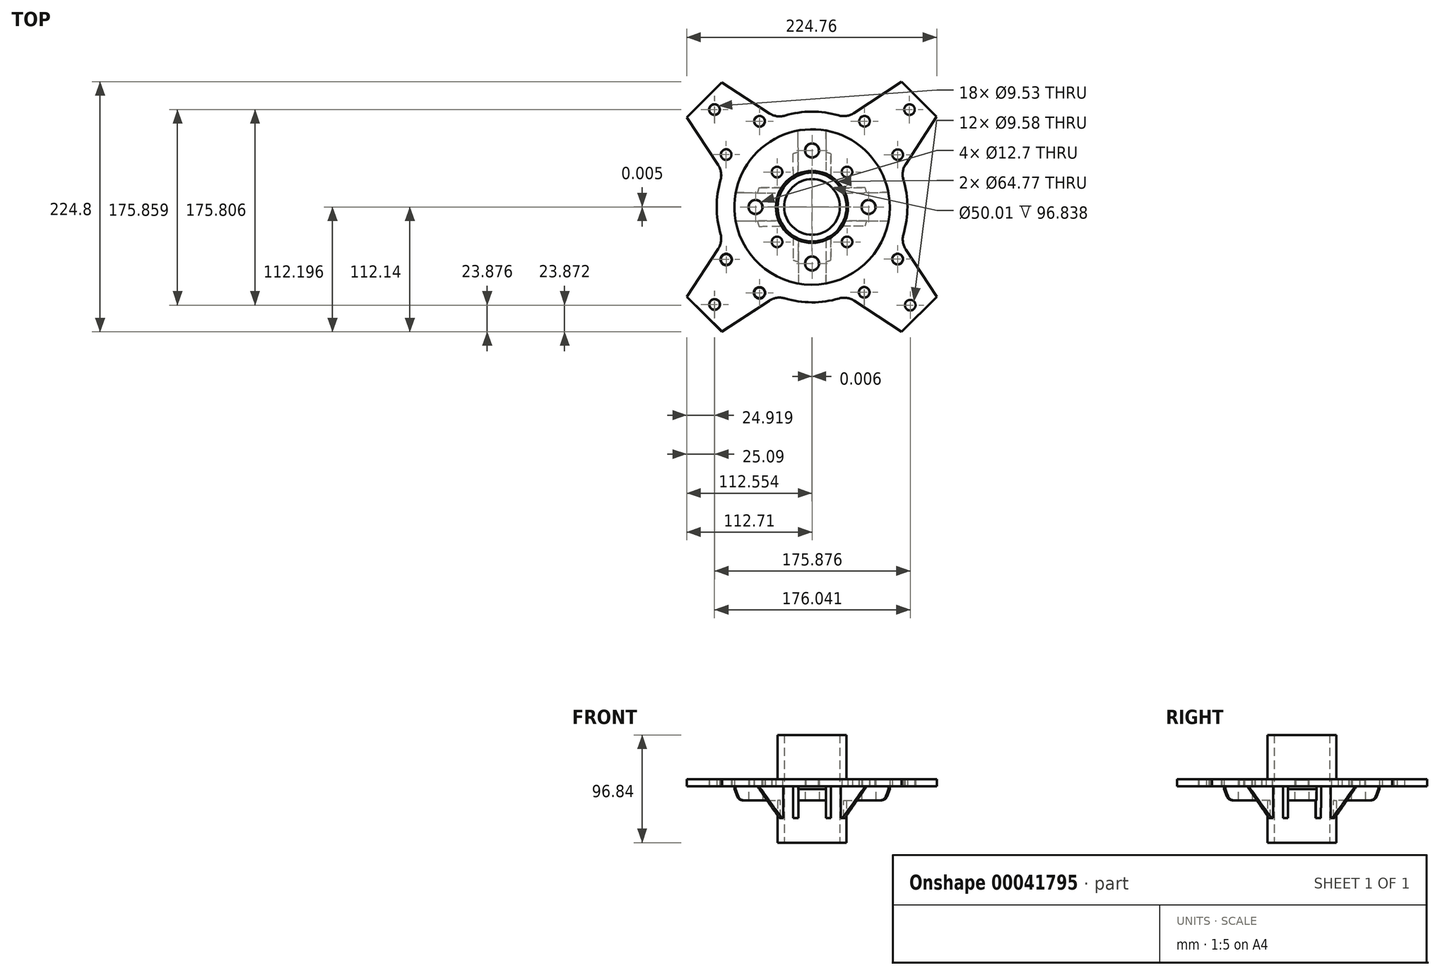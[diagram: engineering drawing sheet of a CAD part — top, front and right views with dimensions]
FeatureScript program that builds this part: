
annotation { "Feature Type Name" : "Feature", "Feature Type Description" : "" }
export const myFeature = defineFeature(function(context is Context, id is Id, definition is map)
    precondition{}
    {
        {
            var Q0;
            Q0=qCreatedBy(makeId("Top.planeOp"),FACE);
            var sketch = newSketch(context, id + "F0", { "sketchPlane" : qUnion([Q0])});
            skCircle(sketch, "E0", {"center": v(0, 0) * mm, "radius": 30.96 * mm});
            skCircle(sketch, "E1", {"center": v(0, 0) * mm, "radius": 25 * mm});
            skCircle(sketch, "E2", {"center": v(0, 0) * mm, "radius": 69.85 * mm});
            skArc(sketch, "E3", {"start": v(-47.7, 17.46) * mm, "mid": v(-48.5, 15.1) * mm, "end": v(-49.19, 12.7) * mm});
            skCircle(sketch, "E4", {"center": v(50.8, 0) * mm, "radius": 6.35 * mm});
            skCircle(sketch, "E5", {"center": v(0, -50.8) * mm, "radius": 6.35 * mm});
            skCircle(sketch, "E6", {"center": v(0, 50.8) * mm, "radius": 6.35 * mm});
            skCircle(sketch, "E7", {"center": v(-50.8, 0) * mm, "radius": 6.35 * mm});
            skArc(sketch, "E8.0", {"start": v(-62.18, 12.9) * mm, "mid": v(-63.5, 0.26) * mm, "end": v(-62.28, -12.38) * mm});
            skLineSegment(sketch, "E9.0", {"start": v(-68.74, -12.38) * mm, "end": v(-28.37, -12.38) * mm});
            skLineSegment(sketch, "E10.0", {"start": v(-68.63, 13) * mm, "end": v(-28.37, 12.38) * mm});
            skLineSegment(sketch, "E11.0", {"start": v(-13, 68.63) * mm, "end": v(-12.38, 28.37) * mm});
            skLineSegment(sketch, "E12.0", {"start": v(12.38, 68.74) * mm, "end": v(12.38, 28.37) * mm});
            skLineSegment(sketch, "E13.trimOffspring", {"start": v(28.37, -12.38) * mm, "end": v(68.74, -12.38) * mm});
            skLineSegment(sketch, "E14.trimOffspring", {"start": v(28.37, 12.38) * mm, "end": v(68.6, 13.19) * mm});
            skLineSegment(sketch, "E15.trimOffspring", {"start": v(12.38, -28.37) * mm, "end": v(12.38, -68.74) * mm});
            skLineSegment(sketch, "E16.trimOffspring", {"start": v(-12.26, -28.42) * mm, "end": v(-12.26, -68.77) * mm});
            skLineSegment(sketch, "E17.0", {"start": v(25.85, 17.04) * mm, "end": v(47.7, 17.48) * mm});
            skLineSegment(sketch, "E18.0", {"start": v(25.85, -17.04) * mm, "end": v(47.86, -17.04) * mm});
            skLineSegment(sketch, "E19.0", {"start": v(17.04, -25.85) * mm, "end": v(17.04, -47.86) * mm});
            skLineSegment(sketch, "E20.0", {"start": v(-17.04, -25.85) * mm, "end": v(-17.04, -47.86) * mm});
            skLineSegment(sketch, "E21.0", {"start": v(17.04, 47.86) * mm, "end": v(17.04, 25.85) * mm});
            skLineSegment(sketch, "E22.trimOffspring", {"start": v(-47.7, 17.46) * mm, "end": v(-25.56, 17.46) * mm});
            skLineSegment(sketch, "E23.trimOffspring", {"start": v(-47.7, -17.48) * mm, "end": v(-25.85, -17.04) * mm});
            skLineSegment(sketch, "E24.trimOffspring", {"start": v(-17.48, 47.7) * mm, "end": v(-17.04, 25.85) * mm});
            skArc(sketch, "E25.trimOffspring", {"start": v(-12.26, -62.3) * mm, "mid": v(0.06, -63.5) * mm, "end": v(12.38, -62.28) * mm});
            skArc(sketch, "E26.trimOffspring", {"start": v(-17.04, -47.86) * mm, "mid": v(-14.67, -48.64) * mm, "end": v(-12.26, -49.3) * mm});
            skArc(sketch, "E27.trimOffspring", {"start": v(62.28, -12.38) * mm, "mid": v(63.5, 0.34) * mm, "end": v(62.14, 13.06) * mm});
            skArc(sketch, "E28.trimOffspring", {"start": v(47.86, -17.04) * mm, "mid": v(48.62, -14.73) * mm, "end": v(49.27, -12.38) * mm});
            skArc(sketch, "E29.trimOffspring", {"start": v(12.38, 62.28) * mm, "mid": v(-0.26, 63.5) * mm, "end": v(-12.9, 62.18) * mm});
            skArc(sketch, "E30.trimOffspring", {"start": v(17.04, 47.86) * mm, "mid": v(14.73, 48.62) * mm, "end": v(12.38, 49.27) * mm});
            skArc(sketch, "E31.trimOffspring", {"start": v(-49.27, -12.38) * mm, "mid": v(-48.55, -14.95) * mm, "end": v(-47.7, -17.48) * mm});
            skArc(sketch, "E32.trimOffspring", {"start": v(12.38, -49.27) * mm, "mid": v(14.73, -48.62) * mm, "end": v(17.04, -47.86) * mm});
            skArc(sketch, "E33.trimOffspring", {"start": v(49.16, 12.8) * mm, "mid": v(48.49, 15.15) * mm, "end": v(47.7, 17.48) * mm});
            skArc(sketch, "E34.trimOffspring", {"start": v(-12.7, 49.19) * mm, "mid": v(-15.1, 48.5) * mm, "end": v(-17.48, 47.7) * mm});
            skSolve(sketch);
        }
        {
            var Q0;
            Q0=qCreatedBy(makeId("Top.planeOp"),FACE);
            var sketch = newSketch(context, id + "F1", { "sketchPlane" : qUnion([Q0])});
            skCircle(sketch, "E35", {"center": v(-77.25, 47.13) * mm, "radius": 4.76 * mm});
            skCircle(sketch, "E36", {"center": v(-0.16, 0.06) * mm, "radius": 32.39 * mm});
            skLineSegment(sketch, "E37", {"start": v(100.22, 100.2) * mm, "end": v(-102.82, -102.8) * mm, "construction": true});
            skCircle(sketch, "E38.0.MirrorC", {"center": v(-47.21, -77.17) * mm, "radius": 5.16 * mm});
            skLineSegment(sketch, "E39", {"start": v(-103.21, 102.97) * mm, "end": v(98.5, -98.33) * mm, "construction": true});
            skCircle(sketch, "E40.0.MirrorC", {"center": v(-77.18, -47.22) * mm, "radius": 5.16 * mm});
            skCircle(sketch, "E41.0.MirrorC", {"center": v(-87.7, -87.7) * mm, "radius": 4.76 * mm});
            skCircle(sketch, "E42", {"center": v(-87.8, 87.6) * mm, "radius": 4.76 * mm});
            skCircle(sketch, "E43", {"center": v(-47.3, 77.09) * mm, "radius": 4.76 * mm});
            skCircle(sketch, "E44", {"center": v(77, 47.02) * mm, "radius": 4.76 * mm});
            skCircle(sketch, "E45", {"center": v(87.56, 87.54) * mm, "radius": 4.76 * mm});
            skCircle(sketch, "E46", {"center": v(47.11, 77.06) * mm, "radius": 4.76 * mm});
            skLineSegment(sketch, "E47", {"start": v(90.92, 90.91) * mm, "end": v(95.62, 95.6) * mm});
            skCircle(sketch, "E48", {"center": v(46.8, -76.66) * mm, "radius": 4.76 * mm});
            skCircle(sketch, "E49", {"center": v(76.84, -46.79) * mm, "radius": 4.76 * mm});
            skCircle(sketch, "E50", {"center": v(88.25, -88.26) * mm, "radius": 4.76 * mm});
            skLineSegment(sketch, "E51", {"start": v(80.53, -112.13) * mm, "end": v(112.05, -80.8) * mm});
            skPoint(sketch, "E52", {"position": v(-81.28, -112.08) * mm});
            skPoint(sketch, "E53", {"position": v(-112.71, -80.65) * mm});
            skLineSegment(sketch, "E54", {"start": v(-112.71, -80.65) * mm, "end": v(-81.28, -112.08) * mm});
            skPoint(sketch, "E55", {"position": v(-112.67, 80.67) * mm});
            skPoint(sketch, "E56", {"position": v(-81.24, 112.1) * mm});
            skLineSegment(sketch, "E57", {"start": v(-81.24, 112.1) * mm, "end": v(-112.67, 80.67) * mm});
            skPoint(sketch, "E58", {"position": v(80.48, 112.66) * mm});
            skLineSegment(sketch, "E59", {"start": v(80.48, 112.66) * mm, "end": v(111.83, 81.15) * mm});
            skPoint(sketch, "E60", {"position": v(111.83, 81.15) * mm});
            skPoint(sketch, "E61", {"position": v(112.05, -80.8) * mm});
            skPoint(sketch, "E62", {"position": v(80.53, -112.13) * mm});
            skCircle(sketch, "E63", {"center": v(-0.16, 0.06) * mm, "radius": 50.8 * mm, "construction": true});
            skLineSegment(sketch, "E64", {"start": v(0, -85.66) * mm, "end": v(0, 97.9) * mm, "construction": true});
            skLineSegment(sketch, "E65", {"start": v(-85.88, 0) * mm, "end": v(116, 0) * mm, "construction": true});
            skLineSegment(sketch, "E66", {"start": v(112.05, -80.8) * mm, "end": v(84.2, -38.16) * mm});
            skLineSegment(sketch, "E67", {"start": v(80.53, -112.13) * mm, "end": v(37.93, -84.28) * mm});
            skLineSegment(sketch, "E68", {"start": v(-112.67, 80.67) * mm, "end": v(-84.39, 37.74) * mm});
            skLineSegment(sketch, "E69", {"start": v(-38.3, 84.15) * mm, "end": v(-81.24, 112.1) * mm});
            skLineSegment(sketch, "E70", {"start": v(80.48, 112.66) * mm, "end": v(37.56, 84.43) * mm});
            skLineSegment(sketch, "E71", {"start": v(-112.71, -80.65) * mm, "end": v(-84.42, -37.59) * mm});
            skLineSegment(sketch, "E72", {"start": v(-81.28, -112.08) * mm, "end": v(-38.38, -84.13) * mm});
            skLineSegment(sketch, "E73", {"start": v(84.1, 38.46) * mm, "end": v(111.83, 81.15) * mm});
            skArc(sketch, "E74", {"start": v(-24.55, -82.13) * mm, "mid": v(-0.2, -85.72) * mm, "end": v(24.16, -82.25) * mm});
            skArc(sketch, "E75.trimOffspring", {"start": v(-82.3, 23.96) * mm, "mid": v(-85.72, 0.06) * mm, "end": v(-82.34, -23.85) * mm});
            skArc(sketch, "E76.filletArc", {"start": v(-82.3, 23.96) * mm, "mid": v(-81.83, 31.08) * mm, "end": v(-84.39, 37.74) * mm});
            skArc(sketch, "E77.filletArc", {"start": v(-84.42, -37.59) * mm, "mid": v(-81.87, -30.95) * mm, "end": v(-82.34, -23.85) * mm});
            skArc(sketch, "E78.filletArc", {"start": v(-24.55, -82.13) * mm, "mid": v(-31.69, -81.6) * mm, "end": v(-38.38, -84.13) * mm});
            skArc(sketch, "E79.trimOffspring", {"start": v(23.82, 82.35) * mm, "mid": v(-0.35, 85.72) * mm, "end": v(-24.49, 82.15) * mm});
            skArc(sketch, "E80.trimOffspring", {"start": v(82.2, -24.36) * mm, "mid": v(85.72, 0.15) * mm, "end": v(82.1, 24.64) * mm});
            skArc(sketch, "E81.filletArc", {"start": v(37.93, -84.28) * mm, "mid": v(31.27, -81.76) * mm, "end": v(24.16, -82.25) * mm});
            skArc(sketch, "E82.filletArc", {"start": v(82.2, -24.36) * mm, "mid": v(81.68, -31.48) * mm, "end": v(84.2, -38.16) * mm});
            skArc(sketch, "E83.filletArc", {"start": v(84.1, 38.46) * mm, "mid": v(81.58, 31.77) * mm, "end": v(82.1, 24.64) * mm});
            skArc(sketch, "E84.filletArc", {"start": v(23.82, 82.35) * mm, "mid": v(30.92, 81.88) * mm, "end": v(37.56, 84.43) * mm});
            skArc(sketch, "E85.filletArc", {"start": v(-38.3, 84.15) * mm, "mid": v(-31.6, 81.63) * mm, "end": v(-24.49, 82.15) * mm});
            skCircle(sketch, "E86", {"center": v(0, 0) * mm, "radius": 44.45 * mm, "construction": true});
            skPoint(sketch, "E87", {"position": v(31.45, -31.42) * mm});
            skPoint(sketch, "E88", {"position": v(-31.43, -31.43) * mm});
            skPoint(sketch, "E89", {"position": v(31.43, 31.43) * mm});
            skPoint(sketch, "E90", {"position": v(-31.48, 31.38) * mm});
            skCircle(sketch, "E91", {"center": v(-31.48, 31.38) * mm, "radius": 4.76 * mm});
            skCircle(sketch, "E92", {"center": v(31.45, -31.42) * mm, "radius": 4.76 * mm});
            skCircle(sketch, "E93", {"center": v(31.43, 31.43) * mm, "radius": 4.76 * mm});
            skCircle(sketch, "E94", {"center": v(-31.43, -31.45) * mm, "radius": 4.76 * mm});
            skCircle(sketch, "E95", {"center": v(0, 0) * mm, "radius": 123.83 * mm, "construction": true});
            skCircle(sketch, "E96", {"center": v(0, 0) * mm, "radius": 136.53 * mm, "construction": true});
            skCircle(sketch, "E97", {"center": v(0, 0) * mm, "radius": 90.49 * mm, "construction": true});
            skSolve(sketch);
        }
        {
            var Q0;
            Q0=qCreatedBy(makeId("Top.planeOp"),FACE);
            var sketch = newSketch(context, id + "F2", { "sketchPlane" : qUnion([Q0])});
            skCircle(sketch, "E98", {"center": v(-0.15, 0.06) * mm, "radius": 32.39 * mm});
            skLineSegment(sketch, "E99", {"start": v(100.23, 100.2) * mm, "end": v(-102.81, -102.81) * mm, "construction": true});
            skLineSegment(sketch, "E100", {"start": v(-119.3, 119.07) * mm, "end": v(108.26, -108) * mm, "construction": true});
            skLineSegment(sketch, "E101", {"start": v(90.93, 90.9) * mm, "end": v(93.76, 93.73) * mm});
            skLineSegment(sketch, "E102", {"start": v(80.53, -112.14) * mm, "end": v(112.05, -80.8) * mm});
            skPoint(sketch, "E103", {"position": v(-80.94, -111.87) * mm});
            skPoint(sketch, "E104", {"position": v(-112.71, -80.67) * mm});
            skLineSegment(sketch, "E105", {"start": v(-112.71, -80.67) * mm, "end": v(-80.94, -111.87) * mm});
            skPoint(sketch, "E106", {"position": v(-112.5, 80.56) * mm});
            skPoint(sketch, "E107", {"position": v(-81.07, 112) * mm});
            skLineSegment(sketch, "E108", {"start": v(-81.07, 112) * mm, "end": v(-112.5, 80.56) * mm});
            skPoint(sketch, "E109", {"position": v(80.49, 112.66) * mm});
            skLineSegment(sketch, "E110", {"start": v(80.49, 112.66) * mm, "end": v(111.84, 81.15) * mm});
            skCircle(sketch, "E111", {"center": v(0, 50.8) * mm, "radius": 5.56 * mm});
            skCircle(sketch, "E112", {"center": v(50.8, 0) * mm, "radius": 5.56 * mm});
            skCircle(sketch, "E113", {"center": v(0, -50.8) * mm, "radius": 5.56 * mm});
            skCircle(sketch, "E114", {"center": v(-50.8, 0) * mm, "radius": 5.56 * mm});
            skPoint(sketch, "E115", {"position": v(111.84, 81.15) * mm});
            skPoint(sketch, "E116", {"position": v(112.05, -80.8) * mm});
            skPoint(sketch, "E117", {"position": v(80.53, -112.14) * mm});
            skCircle(sketch, "E118", {"center": v(-0.15, 0.06) * mm, "radius": 50.8 * mm, "construction": true});
            skLineSegment(sketch, "E119", {"start": v(0, -85.67) * mm, "end": v(0, 97.9) * mm, "construction": true});
            skLineSegment(sketch, "E120", {"start": v(-85.87, 0) * mm, "end": v(116.01, 0) * mm, "construction": true});
            skLineSegment(sketch, "E121", {"start": v(112.05, -80.8) * mm, "end": v(84.22, -38.16) * mm});
            skLineSegment(sketch, "E122", {"start": v(80.53, -112.14) * mm, "end": v(37.94, -84.29) * mm});
            skLineSegment(sketch, "E123", {"start": v(-112.5, 80.56) * mm, "end": v(-84.37, 37.72) * mm});
            skLineSegment(sketch, "E124", {"start": v(-38.29, 84.15) * mm, "end": v(-81.07, 112) * mm});
            skLineSegment(sketch, "E125", {"start": v(80.49, 112.66) * mm, "end": v(37.57, 84.43) * mm});
            skLineSegment(sketch, "E126", {"start": v(-112.71, -80.67) * mm, "end": v(-84.4, -37.6) * mm});
            skLineSegment(sketch, "E127", {"start": v(-80.94, -111.87) * mm, "end": v(-38.37, -84.14) * mm});
            skLineSegment(sketch, "E128", {"start": v(84.1, 38.46) * mm, "end": v(111.84, 81.15) * mm});
            skArc(sketch, "E129", {"start": v(-24.55, -82.14) * mm, "mid": v(-0.2, -85.73) * mm, "end": v(24.17, -82.25) * mm});
            skArc(sketch, "E130.trimOffspring", {"start": v(-82.3, 23.96) * mm, "mid": v(-85.72, 0.06) * mm, "end": v(-82.34, -23.85) * mm});
            skArc(sketch, "E131.filletArc", {"start": v(-82.3, 23.96) * mm, "mid": v(-81.82, 31.06) * mm, "end": v(-84.37, 37.72) * mm});
            skArc(sketch, "E132.filletArc", {"start": v(-84.4, -37.6) * mm, "mid": v(-81.87, -30.95) * mm, "end": v(-82.34, -23.85) * mm});
            skArc(sketch, "E133.filletArc", {"start": v(-24.55, -82.14) * mm, "mid": v(-31.68, -81.61) * mm, "end": v(-38.37, -84.14) * mm});
            skArc(sketch, "E134.trimOffspring", {"start": v(23.82, 82.35) * mm, "mid": v(-0.34, 85.72) * mm, "end": v(-24.48, 82.15) * mm});
            skArc(sketch, "E135.trimOffspring", {"start": v(82.2, -24.36) * mm, "mid": v(85.73, 0.14) * mm, "end": v(82.12, 24.63) * mm});
            skArc(sketch, "E136.filletArc", {"start": v(37.94, -84.29) * mm, "mid": v(31.27, -81.76) * mm, "end": v(24.17, -82.25) * mm});
            skArc(sketch, "E137.filletArc", {"start": v(82.2, -24.36) * mm, "mid": v(81.69, -31.48) * mm, "end": v(84.22, -38.16) * mm});
            skArc(sketch, "E138.filletArc", {"start": v(84.1, 38.46) * mm, "mid": v(81.58, 31.76) * mm, "end": v(82.12, 24.63) * mm});
            skArc(sketch, "E139.filletArc", {"start": v(23.82, 82.35) * mm, "mid": v(30.92, 81.88) * mm, "end": v(37.57, 84.43) * mm});
            skArc(sketch, "E140.filletArc", {"start": v(-38.29, 84.15) * mm, "mid": v(-31.6, 81.63) * mm, "end": v(-24.48, 82.15) * mm});
            skCircle(sketch, "E141", {"center": v(0, 50.8) * mm, "radius": 6.35 * mm});
            skCircle(sketch, "E142", {"center": v(-50.8, 0) * mm, "radius": 6.35 * mm});
            skCircle(sketch, "E143", {"center": v(0, -50.8) * mm, "radius": 6.35 * mm});
            skCircle(sketch, "E144", {"center": v(50.8, 0) * mm, "radius": 6.35 * mm});
            skCircle(sketch, "E145", {"center": v(-77.24, 47.12) * mm, "radius": 4.79 * mm});
            skCircle(sketch, "E146", {"center": v(-77.17, -47.22) * mm, "radius": 4.79 * mm});
            skCircle(sketch, "E147", {"center": v(-47.2, -77.17) * mm, "radius": 4.79 * mm});
            skCircle(sketch, "E148", {"center": v(46.95, -76.76) * mm, "radius": 4.79 * mm});
            skCircle(sketch, "E149", {"center": v(77, -46.88) * mm, "radius": 4.79 * mm});
            skCircle(sketch, "E150", {"center": v(77, 47.02) * mm, "radius": 4.79 * mm});
            skCircle(sketch, "E151", {"center": v(88.26, -88.27) * mm, "radius": 4.79 * mm});
            skCircle(sketch, "E152", {"center": v(-87.54, -87.58) * mm, "radius": 4.79 * mm});
            skCircle(sketch, "E153", {"center": v(-87.62, 87.48) * mm, "radius": 4.79 * mm});
            skCircle(sketch, "E154", {"center": v(-47.14, 77) * mm, "radius": 4.79 * mm});
            skCircle(sketch, "E155", {"center": v(47.12, 77.05) * mm, "radius": 4.79 * mm});
            skCircle(sketch, "E156", {"center": v(87.56, 87.54) * mm, "radius": 4.79 * mm});
            skCircle(sketch, "E157", {"center": v(0, 0) * mm, "radius": 44.45 * mm, "construction": true});
            skPoint(sketch, "E158", {"position": v(-31.45, 31.4) * mm});
            skPoint(sketch, "E159", {"position": v(31.44, 31.42) * mm});
            skPoint(sketch, "E160", {"position": v(31.48, -31.4) * mm});
            skPoint(sketch, "E161", {"position": v(-31.43, -31.44) * mm});
            skCircle(sketch, "E162", {"center": v(31.43, 31.43) * mm, "radius": 4.76 * mm});
            skCircle(sketch, "E163", {"center": v(-31.45, 31.4) * mm, "radius": 4.76 * mm});
            skCircle(sketch, "E164", {"center": v(-31.43, -31.43) * mm, "radius": 4.76 * mm});
            skCircle(sketch, "E165", {"center": v(31.48, -31.4) * mm, "radius": 4.76 * mm});
            skCircle(sketch, "E166", {"center": v(0, 0) * mm, "radius": 90.49 * mm, "construction": true});
            skCircle(sketch, "E167", {"center": v(0, 0) * mm, "radius": 123.83 * mm, "construction": true});
            skCircle(sketch, "E168", {"center": v(0, 0) * mm, "radius": 136.53 * mm, "construction": true});
            skPoint(sketch, "E169", {"position": v(-96.62, 96.45) * mm});
            skPoint(sketch, "E170", {"position": v(96.5, -96.27) * mm});
            skSolve(sketch);
        }
        {
            var Q0;
            {var subQ4=sQuery(id+"F0.wireOp",EDGE,"E3");Q0=makeQuery(id+"F0.imprint","IMPRINT",FACE,{"disambiguationData":[TD([[makeQuery(id+"F0.imprint","IMPRINT",EDGE,{"derivedFrom":subQ4}),-1.0]])]});}
            var Q1;
            {var subQ3=sQuery(id+"F0.wireOp",EDGE,"E8.0");Q1=makeQuery(id+"F0.imprint","IMPRINT",FACE,{"disambiguationData":[TD([[makeQuery(id+"F0.imprint","IMPRINT",EDGE,{"derivedFrom":subQ3}),-1.0]])]});}
            var Q2;
            {var subQ10=sQuery(id+"F0.wireOp",EDGE,"E20.0");Q2=makeQuery(id+"F0.imprint","IMPRINT",FACE,{"disambiguationData":[TD([[makeQuery(id+"F0.imprint","IMPRINT",EDGE,{"derivedFrom":subQ10}),-1.0]])]});}
            var Q3;
            {var subQ0=sQuery(id+"F0.wireOp",EDGE,"E25.trimOffspring");Q3=makeQuery(id+"F0.imprint","IMPRINT",FACE,{"disambiguationData":[TD([[makeQuery(id+"F0.imprint","IMPRINT",EDGE,{"derivedFrom":subQ0}),-1.0]])]});}
            var Q4;
            {var subQ2=sQuery(id+"F0.wireOp",EDGE,"E18.0");Q4=makeQuery(id+"F0.imprint","IMPRINT",FACE,{"disambiguationData":[TD([[makeQuery(id+"F0.imprint","IMPRINT",EDGE,{"derivedFrom":subQ2}),-1.0]])]});}
            var Q5;
            {var subQ0=sQuery(id+"F0.wireOp",EDGE,"E27.trimOffspring");Q5=makeQuery(id+"F0.imprint","IMPRINT",FACE,{"disambiguationData":[TD([[makeQuery(id+"F0.imprint","IMPRINT",EDGE,{"derivedFrom":subQ0}),-1.0]])]});}
            var Q6;
            {var subQ3=sQuery(id+"F0.wireOp",EDGE,"E17.0");Q6=makeQuery(id+"F0.imprint","IMPRINT",FACE,{"disambiguationData":[TD([[makeQuery(id+"F0.imprint","IMPRINT",EDGE,{"derivedFrom":subQ3}),1.0]])]});}
            var Q7;
            {var subQ0=sQuery(id+"F0.wireOp",EDGE,"E29.trimOffspring");Q7=makeQuery(id+"F0.imprint","IMPRINT",FACE,{"disambiguationData":[TD([[makeQuery(id+"F0.imprint","IMPRINT",EDGE,{"derivedFrom":subQ0}),-1.0]])]});}
            var Q8;
            Q8=makeQuery(id+"F0.imprint","IMPRINT",FACE,{"disambiguationData":[TD([[makeQuery(id+"F0.imprint","IMPRINT",EDGE,{"derivedFrom":sQuery(id+"F0.wireOp",EDGE,"E7")}),-1.0]])]});
            var Q9;
            Q9=makeQuery(id+"F0.imprint","IMPRINT",FACE,{"disambiguationData":[TD([[makeQuery(id+"F0.imprint","IMPRINT",EDGE,{"derivedFrom":sQuery(id+"F0.wireOp",EDGE,"E6")}),-1.0]])]});
            var Q10;
            Q10=makeQuery(id+"F0.imprint","IMPRINT",FACE,{"disambiguationData":[TD([[makeQuery(id+"F0.imprint","IMPRINT",EDGE,{"derivedFrom":sQuery(id+"F0.wireOp",EDGE,"E4")}),-1.0]])]});
            var Q11;
            Q11=makeQuery(id+"F0.imprint","IMPRINT",FACE,{"disambiguationData":[TD([[makeQuery(id+"F0.imprint","IMPRINT",EDGE,{"derivedFrom":sQuery(id+"F0.wireOp",EDGE,"E5")}),-1.0]])]});
            var Q12;
            {var subQ3=sQuery(id+"F0.wireOp",EDGE,"E3");Q12=makeQuery(id+"F0.imprint","IMPRINT",FACE,{"disambiguationData":[TD([[makeQuery(id+"F0.imprint","IMPRINT",EDGE,{"derivedFrom":subQ3}),1.0]])]});}
            var Q13;
            {var subQ1=sQuery(id+"F0.wireOp",EDGE,"E23.trimOffspring");Q13=makeQuery(id+"F0.imprint","IMPRINT",FACE,{"disambiguationData":[TD([[makeQuery(id+"F0.imprint","IMPRINT",EDGE,{"derivedFrom":subQ1}),1.0]])]});}
            var Q14;
            {var subQ1=sQuery(id+"F0.wireOp",EDGE,"E20.0");Q14=makeQuery(id+"F0.imprint","IMPRINT",FACE,{"disambiguationData":[TD([[makeQuery(id+"F0.imprint","IMPRINT",EDGE,{"derivedFrom":subQ1}),1.0]])]});}
            var Q15;
            {var subQ0=sQuery(id+"F0.wireOp",EDGE,"E19.0");Q15=makeQuery(id+"F0.imprint","IMPRINT",FACE,{"disambiguationData":[TD([[makeQuery(id+"F0.imprint","IMPRINT",EDGE,{"derivedFrom":subQ0}),-1.0]])]});}
            var Q16;
            {var subQ1=sQuery(id+"F0.wireOp",EDGE,"E18.0");Q16=makeQuery(id+"F0.imprint","IMPRINT",FACE,{"disambiguationData":[TD([[makeQuery(id+"F0.imprint","IMPRINT",EDGE,{"derivedFrom":subQ1}),1.0]])]});}
            var Q17;
            {var subQ1=sQuery(id+"F0.wireOp",EDGE,"E17.0");Q17=makeQuery(id+"F0.imprint","IMPRINT",FACE,{"disambiguationData":[TD([[makeQuery(id+"F0.imprint","IMPRINT",EDGE,{"derivedFrom":subQ1}),-1.0]])]});}
            var Q18;
            {var subQ1=sQuery(id+"F0.wireOp",EDGE,"E21.0");Q18=makeQuery(id+"F0.imprint","IMPRINT",FACE,{"disambiguationData":[TD([[makeQuery(id+"F0.imprint","IMPRINT",EDGE,{"derivedFrom":subQ1}),-1.0]])]});}
            var Q19;
            {var subQ1=sQuery(id+"F0.wireOp",EDGE,"E24.trimOffspring");Q19=makeQuery(id+"F0.imprint","IMPRINT",FACE,{"disambiguationData":[TD([[makeQuery(id+"F0.imprint","IMPRINT",EDGE,{"derivedFrom":subQ1}),1.0]])]});}
            var Q20;
            Q20=makeQuery(id+"F0.imprint","IMPRINT",FACE,{"disambiguationData":[TD([[makeQuery(id+"F0.imprint","IMPRINT",EDGE,{"derivedFrom":sQuery(id+"F0.wireOp",EDGE,"E1")}),-1.0]])]});
            extrude(context, id + "F3", {"entities" : qUnion([Q0, Q1, Q2, Q3, Q4, Q5, Q6, Q7, Q8, Q9, Q10, Q11, Q12, Q13, Q14, Q15, Q16, Q17, Q18, Q19, Q20]), "depth" : 6.35 * mm});
        }
        {
            var Q0;
            Q0=makeQuery(id+"F0.imprint","IMPRINT",FACE,{"disambiguationData":[TD([[makeQuery(id+"F0.imprint","IMPRINT",EDGE,{"derivedFrom":sQuery(id+"F0.wireOp",EDGE,"E7")}),-1.0]])]});
            var Q1;
            Q1=makeQuery(id+"F0.imprint","IMPRINT",FACE,{"disambiguationData":[TD([[makeQuery(id+"F0.imprint","IMPRINT",EDGE,{"derivedFrom":sQuery(id+"F0.wireOp",EDGE,"E6")}),-1.0]])]});
            var Q2;
            Q2=makeQuery(id+"F0.imprint","IMPRINT",FACE,{"disambiguationData":[TD([[makeQuery(id+"F0.imprint","IMPRINT",EDGE,{"derivedFrom":sQuery(id+"F0.wireOp",EDGE,"E4")}),-1.0]])]});
            var Q3;
            Q3=makeQuery(id+"F0.imprint","IMPRINT",FACE,{"disambiguationData":[TD([[makeQuery(id+"F0.imprint","IMPRINT",EDGE,{"derivedFrom":sQuery(id+"F0.wireOp",EDGE,"E5")}),-1.0]])]});
            var Q4;
            {var subQ0=sQuery(id+"F0.wireOp",EDGE,"E25.trimOffspring");Q4=makeQuery(id+"F0.imprint","IMPRINT",FACE,{"disambiguationData":[TD([[makeQuery(id+"F0.imprint","IMPRINT",EDGE,{"derivedFrom":subQ0}),-1.0]])]});}
            var Q5;
            {var subQ3=sQuery(id+"F0.wireOp",EDGE,"E8.0");Q5=makeQuery(id+"F0.imprint","IMPRINT",FACE,{"disambiguationData":[TD([[makeQuery(id+"F0.imprint","IMPRINT",EDGE,{"derivedFrom":subQ3}),-1.0]])]});}
            var Q6;
            {var subQ0=sQuery(id+"F0.wireOp",EDGE,"E27.trimOffspring");Q6=makeQuery(id+"F0.imprint","IMPRINT",FACE,{"disambiguationData":[TD([[makeQuery(id+"F0.imprint","IMPRINT",EDGE,{"derivedFrom":subQ0}),-1.0]])]});}
            var Q7;
            {var subQ0=sQuery(id+"F0.wireOp",EDGE,"E29.trimOffspring");Q7=makeQuery(id+"F0.imprint","IMPRINT",FACE,{"disambiguationData":[TD([[makeQuery(id+"F0.imprint","IMPRINT",EDGE,{"derivedFrom":subQ0}),-1.0]])]});}
            extrude(context, id + "F4", {"entities" : qUnion([Q0, Q1, Q2, Q3, Q4, Q5, Q6, Q7]), "operationType" : NewBodyOperationType.ADD, "oppositeDirection" : true, "depth" : 12.7 * mm});
        }
        {
            var Q0;
            {var subQ0=sQuery(id+"F0.wireOp",EDGE,"E2");Q0=makeQuery(id+"F4.opExtrude","CAP_EDGE",EDGE,{"disambiguationData":[OSD([subQ0]),TDD([makeQuery(id+"F0.imprint","IMPRINT",EDGE,{"disambiguationData":[TD([[makeQuery(id+"F0.imprint","INTERSECT",VERTEX,{"derivedFrom":[subQ0,sQuery(id+"F0.wireOp",EDGE,"E11.0")]}),1.0]])],"derivedFrom":subQ0})])],"isStart":false});}
            var Q1;
            {var subQ0=sQuery(id+"F0.wireOp",EDGE,"E2");Q1=makeQuery(id+"F4.opExtrude","CAP_EDGE",EDGE,{"disambiguationData":[OSD([subQ0]),TDD([makeQuery(id+"F0.imprint","IMPRINT",EDGE,{"disambiguationData":[TD([[makeQuery(id+"F0.imprint","INTERSECT",VERTEX,{"derivedFrom":[subQ0,sQuery(id+"F0.wireOp",EDGE,"E13.trimOffspring")]}),-1.0]])],"derivedFrom":subQ0})])],"isStart":false});}
            var Q2;
            {var subQ0=sQuery(id+"F0.wireOp",EDGE,"E2");Q2=makeQuery(id+"F4.opExtrude","CAP_EDGE",EDGE,{"disambiguationData":[OSD([subQ0]),TDD([makeQuery(id+"F0.imprint","IMPRINT",EDGE,{"disambiguationData":[TD([[makeQuery(id+"F0.imprint","INTERSECT",VERTEX,{"derivedFrom":[subQ0,sQuery(id+"F0.wireOp",EDGE,"E15.trimOffspring")]}),1.0]])],"derivedFrom":subQ0})])],"isStart":false});}
            var Q3;
            {var subQ0=sQuery(id+"F0.wireOp",EDGE,"E2");Q3=makeQuery(id+"F4.opExtrude","CAP_EDGE",EDGE,{"disambiguationData":[OSD([subQ0]),TDD([makeQuery(id+"F0.imprint","IMPRINT",EDGE,{"disambiguationData":[TD([[makeQuery(id+"F0.imprint","INTERSECT",VERTEX,{"derivedFrom":[subQ0,sQuery(id+"F0.wireOp",EDGE,"E9.0")]}),1.0]])],"derivedFrom":subQ0})])],"isStart":false});}
            chamfer(context, id + "F5", {"entities" : qUnion([Q0, Q1, Q2, Q3]), "chamferType" : ChamferType.TWO_OFFSETS, "width1" : 10.16 * mm, "oppositeDirection" : false, "width2" : 3.8 * mm});
        }
        {
            var Q0;
            {var subQ0=sQuery(id+"F0.wireOp",EDGE,"E2");var subQ1=sQuery(id+"F0.wireOp",EDGE,"E14.trimOffspring");var subQ2=sQuery(id+"F0.wireOp",EDGE,"E13.trimOffspring");Q0=makeQuery(id+"F5.opChamfer","BLEND_EDGE",EDGE,{"blendedFrom":[makeQuery(id+"F4.opExtrude","CAP_EDGE",EDGE,{"disambiguationData":[OSD([subQ0]),TDD([makeQuery(id+"F0.imprint","IMPRINT",EDGE,{"disambiguationData":[TD([[makeQuery(id+"F0.imprint","INTERSECT",VERTEX,{"derivedFrom":[subQ0,subQ2]}),-1.0]])],"derivedFrom":subQ0})])],"isStart":false}),makeQuery(id+"F4.opExtrude","CAP_FACE",FACE,{"disambiguationData":[OSD([sQuery(id+"F0.wireOp",EDGE,"E0"),subQ0,sQuery(id+"F0.wireOp",EDGE,"E4"),subQ2,subQ1])],"isStart":false})],"blendedInto":[makeQuery(id+"F4.opExtrude","CAP_FACE",FACE,{"disambiguationData":[OSD([sQuery(id+"F0.wireOp",EDGE,"E0"),subQ0,sQuery(id+"F0.wireOp",EDGE,"E4"),subQ2,subQ1])],"isStart":false})]});}
            var Q1;
            {var subQ0=sQuery(id+"F0.wireOp",EDGE,"E2");var subQ1=sQuery(id+"F0.wireOp",EDGE,"E12.0");var subQ2=sQuery(id+"F0.wireOp",EDGE,"E11.0");Q1=makeQuery(id+"F5.opChamfer","BLEND_EDGE",EDGE,{"blendedFrom":[makeQuery(id+"F4.opExtrude","CAP_EDGE",EDGE,{"disambiguationData":[OSD([subQ0]),TDD([makeQuery(id+"F0.imprint","IMPRINT",EDGE,{"disambiguationData":[TD([[makeQuery(id+"F0.imprint","INTERSECT",VERTEX,{"derivedFrom":[subQ0,subQ2]}),1.0]])],"derivedFrom":subQ0})])],"isStart":false}),makeQuery(id+"F4.opExtrude","CAP_FACE",FACE,{"disambiguationData":[OSD([sQuery(id+"F0.wireOp",EDGE,"E0"),subQ0,sQuery(id+"F0.wireOp",EDGE,"E6"),subQ2,subQ1])],"isStart":false})],"blendedInto":[makeQuery(id+"F4.opExtrude","CAP_FACE",FACE,{"disambiguationData":[OSD([sQuery(id+"F0.wireOp",EDGE,"E0"),subQ0,sQuery(id+"F0.wireOp",EDGE,"E6"),subQ2,subQ1])],"isStart":false})]});}
            var Q2;
            {var subQ0=sQuery(id+"F0.wireOp",EDGE,"E2");var subQ1=sQuery(id+"F0.wireOp",EDGE,"E10.0");var subQ2=sQuery(id+"F0.wireOp",EDGE,"E9.0");Q2=makeQuery(id+"F5.opChamfer","BLEND_EDGE",EDGE,{"blendedFrom":[makeQuery(id+"F4.opExtrude","CAP_EDGE",EDGE,{"disambiguationData":[OSD([subQ0]),TDD([makeQuery(id+"F0.imprint","IMPRINT",EDGE,{"disambiguationData":[TD([[makeQuery(id+"F0.imprint","INTERSECT",VERTEX,{"derivedFrom":[subQ0,subQ2]}),1.0]])],"derivedFrom":subQ0})])],"isStart":false}),makeQuery(id+"F4.opExtrude","CAP_FACE",FACE,{"disambiguationData":[OSD([sQuery(id+"F0.wireOp",EDGE,"E0"),subQ0,sQuery(id+"F0.wireOp",EDGE,"E7"),subQ2,subQ1])],"isStart":false})],"blendedInto":[makeQuery(id+"F4.opExtrude","CAP_FACE",FACE,{"disambiguationData":[OSD([sQuery(id+"F0.wireOp",EDGE,"E0"),subQ0,sQuery(id+"F0.wireOp",EDGE,"E7"),subQ2,subQ1])],"isStart":false})]});}
            var Q3;
            {var subQ0=sQuery(id+"F0.wireOp",EDGE,"E2");var subQ1=sQuery(id+"F0.wireOp",EDGE,"E16.trimOffspring");var subQ2=sQuery(id+"F0.wireOp",EDGE,"E15.trimOffspring");Q3=makeQuery(id+"F5.opChamfer","BLEND_EDGE",EDGE,{"blendedFrom":[makeQuery(id+"F4.opExtrude","CAP_EDGE",EDGE,{"disambiguationData":[OSD([subQ0]),TDD([makeQuery(id+"F0.imprint","IMPRINT",EDGE,{"disambiguationData":[TD([[makeQuery(id+"F0.imprint","INTERSECT",VERTEX,{"derivedFrom":[subQ0,subQ2]}),1.0]])],"derivedFrom":subQ0})])],"isStart":false}),makeQuery(id+"F4.opExtrude","CAP_FACE",FACE,{"disambiguationData":[OSD([sQuery(id+"F0.wireOp",EDGE,"E0"),subQ0,sQuery(id+"F0.wireOp",EDGE,"E5"),subQ2,subQ1])],"isStart":false})],"blendedInto":[makeQuery(id+"F4.opExtrude","CAP_FACE",FACE,{"disambiguationData":[OSD([sQuery(id+"F0.wireOp",EDGE,"E0"),subQ0,sQuery(id+"F0.wireOp",EDGE,"E5"),subQ2,subQ1])],"isStart":false})]});}
            fillet(context, id + "F6", {"entities" : qUnion([Q0, Q1, Q2, Q3]), "radius" : 5.08 * mm, "tangentPropagation" : true, "allowEdgeOverflow" : false});
        }
        {
            var Q0;
            Q0=makeQuery(id+"F0.imprint","IMPRINT",FACE,{"disambiguationData":[TD([[makeQuery(id+"F0.imprint","IMPRINT",EDGE,{"derivedFrom":sQuery(id+"F0.wireOp",EDGE,"E1")}),-1.0]])]});
            extrude(context, id + "F7", {"entities" : qUnion([Q0]), "operationType" : NewBodyOperationType.ADD, "depth" : 46.04 * mm, "hasSecondDirection" : true, "secondDirectionOppositeDirection" : true, "secondDirectionDepth" : 50.8 * mm});
        }
        {
            var Q0;
            {var subQ1=sQuery(id+"F0.wireOp",EDGE,"E20.0");Q0=makeQuery(id+"F0.imprint","IMPRINT",FACE,{"disambiguationData":[TD([[makeQuery(id+"F0.imprint","IMPRINT",EDGE,{"derivedFrom":subQ1}),1.0]])]});}
            var Q1;
            {var subQ0=sQuery(id+"F0.wireOp",EDGE,"E19.0");Q1=makeQuery(id+"F0.imprint","IMPRINT",FACE,{"disambiguationData":[TD([[makeQuery(id+"F0.imprint","IMPRINT",EDGE,{"derivedFrom":subQ0}),-1.0]])]});}
            var Q2;
            {var subQ1=sQuery(id+"F0.wireOp",EDGE,"E18.0");Q2=makeQuery(id+"F0.imprint","IMPRINT",FACE,{"disambiguationData":[TD([[makeQuery(id+"F0.imprint","IMPRINT",EDGE,{"derivedFrom":subQ1}),1.0]])]});}
            var Q3;
            {var subQ1=sQuery(id+"F0.wireOp",EDGE,"E17.0");Q3=makeQuery(id+"F0.imprint","IMPRINT",FACE,{"disambiguationData":[TD([[makeQuery(id+"F0.imprint","IMPRINT",EDGE,{"derivedFrom":subQ1}),-1.0]])]});}
            var Q4;
            {var subQ1=sQuery(id+"F0.wireOp",EDGE,"E21.0");Q4=makeQuery(id+"F0.imprint","IMPRINT",FACE,{"disambiguationData":[TD([[makeQuery(id+"F0.imprint","IMPRINT",EDGE,{"derivedFrom":subQ1}),-1.0]])]});}
            var Q5;
            {var subQ1=sQuery(id+"F0.wireOp",EDGE,"E24.trimOffspring");Q5=makeQuery(id+"F0.imprint","IMPRINT",FACE,{"disambiguationData":[TD([[makeQuery(id+"F0.imprint","IMPRINT",EDGE,{"derivedFrom":subQ1}),1.0]])]});}
            var Q6;
            {var subQ3=sQuery(id+"F0.wireOp",EDGE,"E3");Q6=makeQuery(id+"F0.imprint","IMPRINT",FACE,{"disambiguationData":[TD([[makeQuery(id+"F0.imprint","IMPRINT",EDGE,{"derivedFrom":subQ3}),1.0]])]});}
            var Q7;
            {var subQ1=sQuery(id+"F0.wireOp",EDGE,"E23.trimOffspring");Q7=makeQuery(id+"F0.imprint","IMPRINT",FACE,{"disambiguationData":[TD([[makeQuery(id+"F0.imprint","IMPRINT",EDGE,{"derivedFrom":subQ1}),1.0]])]});}
            extrude(context, id + "F8", {"entities" : qUnion([Q0, Q1, Q2, Q3, Q4, Q5, Q6, Q7]), "operationType" : NewBodyOperationType.ADD, "oppositeDirection" : true, "depth" : 28.57 * mm});
        }
        {
            var Q0;
            Q0=makeQuery(id+"F8.opExtrude","CAP_EDGE",EDGE,{"disambiguationData":[OSD([sQuery(id+"F0.wireOp",EDGE,"E30.trimOffspring")])],"isStart":false});
            var Q1;
            Q1=makeQuery(id+"F8.opExtrude","CAP_EDGE",EDGE,{"disambiguationData":[OSD([sQuery(id+"F0.wireOp",EDGE,"E34.trimOffspring")])],"isStart":false});
            var Q2;
            Q2=makeQuery(id+"F8.opExtrude","CAP_EDGE",EDGE,{"disambiguationData":[OSD([sQuery(id+"F0.wireOp",EDGE,"E3")])],"isStart":false});
            var Q3;
            Q3=makeQuery(id+"F8.opExtrude","CAP_EDGE",EDGE,{"disambiguationData":[OSD([sQuery(id+"F0.wireOp",EDGE,"E31.trimOffspring")])],"isStart":false});
            var Q4;
            Q4=makeQuery(id+"F8.opExtrude","CAP_EDGE",EDGE,{"disambiguationData":[OSD([sQuery(id+"F0.wireOp",EDGE,"E33.trimOffspring")])],"isStart":false});
            var Q5;
            Q5=makeQuery(id+"F8.opExtrude","CAP_EDGE",EDGE,{"disambiguationData":[OSD([sQuery(id+"F0.wireOp",EDGE,"E28.trimOffspring")])],"isStart":false});
            var Q6;
            Q6=makeQuery(id+"F8.opExtrude","CAP_EDGE",EDGE,{"disambiguationData":[OSD([sQuery(id+"F0.wireOp",EDGE,"E32.trimOffspring")])],"isStart":false});
            var Q7;
            Q7=makeQuery(id+"F8.opExtrude","CAP_EDGE",EDGE,{"disambiguationData":[OSD([sQuery(id+"F0.wireOp",EDGE,"E26.trimOffspring")])],"isStart":false});
            chamfer(context, id + "F9", {"entities" : qUnion([Q0, Q1, Q2, Q3, Q4, Q5, Q6, Q7]), "chamferType" : ChamferType.TWO_OFFSETS, "width1" : 28.7 * mm, "oppositeDirection" : false, "width2" : 18.8 * mm, "tangentPropagation" : true});
        }
        {
            var Q0;
            Q0=makeQuery(id+"F2.imprint","IMPRINT",FACE,{"disambiguationData":[TD([[makeQuery(id+"F2.imprint","IMPRINT",EDGE,{"derivedFrom":sQuery(id+"F2.wireOp",EDGE,"E98")}),-1.0]])]});
            var Q1;
            Q1=makeQuery(id+"F2.imprint","IMPRINT",FACE,{"disambiguationData":[TD([[makeQuery(id+"F2.imprint","IMPRINT",EDGE,{"derivedFrom":sQuery(id+"F2.wireOp",EDGE,"E111")}),-1.0]])]});
            var Q2;
            Q2=makeQuery(id+"F2.imprint","IMPRINT",FACE,{"disambiguationData":[TD([[makeQuery(id+"F2.imprint","IMPRINT",EDGE,{"derivedFrom":sQuery(id+"F2.wireOp",EDGE,"E112")}),-1.0]])]});
            var Q3;
            Q3=makeQuery(id+"F2.imprint","IMPRINT",FACE,{"disambiguationData":[TD([[makeQuery(id+"F2.imprint","IMPRINT",EDGE,{"derivedFrom":sQuery(id+"F2.wireOp",EDGE,"E113")}),-1.0]])]});
            var Q4;
            Q4=makeQuery(id+"F2.imprint","IMPRINT",FACE,{"disambiguationData":[TD([[makeQuery(id+"F2.imprint","IMPRINT",EDGE,{"derivedFrom":sQuery(id+"F2.wireOp",EDGE,"E114")}),-1.0]])]});
            extrude(context, id + "F10", {"entities" : qUnion([Q0, Q1, Q2, Q3, Q4]), "depth" : 6.35 * mm});
        }
        {
            var Q0;
            Q0=makeQuery(id+"F10.opExtrude","CAP_EDGE",EDGE,{"disambiguationData":[OSD([sQuery(id+"F2.wireOp",EDGE,"E114")])],"isStart":false});
            var Q1;
            Q1=makeQuery(id+"F10.opExtrude","CAP_EDGE",EDGE,{"disambiguationData":[OSD([sQuery(id+"F2.wireOp",EDGE,"E111")])],"isStart":false});
            var Q2;
            Q2=makeQuery(id+"F10.opExtrude","CAP_EDGE",EDGE,{"disambiguationData":[OSD([sQuery(id+"F2.wireOp",EDGE,"E112")])],"isStart":false});
            var Q3;
            Q3=makeQuery(id+"F10.opExtrude","CAP_EDGE",EDGE,{"disambiguationData":[OSD([sQuery(id+"F2.wireOp",EDGE,"E113")])],"isStart":false});
            chamfer(context, id + "F11", {"entities" : qUnion([Q0, Q1, Q2, Q3]), "width" : 0.76 * mm, "tangentPropagation" : true});
        }
        {
            var Q0;
            Q0=makeQuery(id+"F1.imprint","IMPRINT",FACE,{"disambiguationData":[TD([[makeQuery(id+"F1.imprint","IMPRINT",EDGE,{"derivedFrom":sQuery(id+"F1.wireOp",EDGE,"E35")}),-1.0]])]});
            extrude(context, id + "F12", {"entities" : qUnion([Q0]), "depth" : 6.35 * mm});
        }
    });
